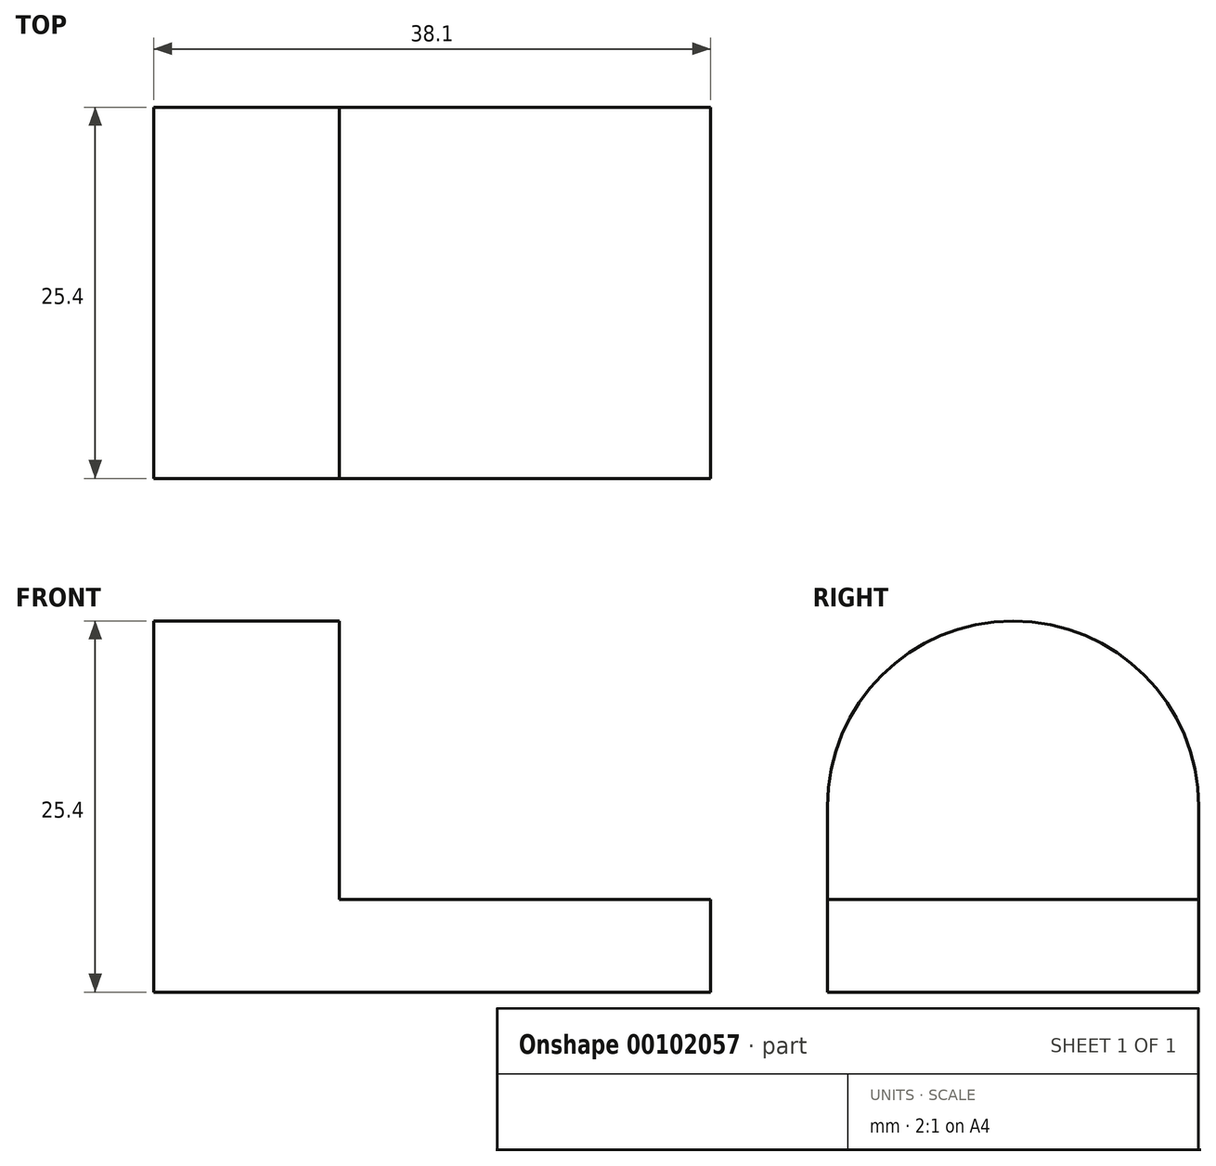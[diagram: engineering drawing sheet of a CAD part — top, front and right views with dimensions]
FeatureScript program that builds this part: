
annotation { "Feature Type Name" : "Feature", "Feature Type Description" : "" }
export const myFeature = defineFeature(function(context is Context, id is Id, definition is map)
    precondition{}
    {
        {
            var Q0;
            Q0=qCreatedBy(makeId("Front.planeOp"),FACE);
            var sketch = newSketch(context, id + "F0", { "sketchPlane" : qUnion([Q0])});
            skLineSegment(sketch, "E0.bottom", {"start": v(0, 0) * mm, "end": v(38.1, 0) * mm});
            skLineSegment(sketch, "E0.top", {"start": v(0, 6.35) * mm, "end": v(38.1, 6.35) * mm});
            skLineSegment(sketch, "E0.left", {"start": v(0, 0) * mm, "end": v(0, 6.35) * mm});
            skLineSegment(sketch, "E0.right", {"start": v(38.1, 0) * mm, "end": v(38.1, 6.35) * mm});
            skSolve(sketch);
        }
        {
            var Q0;
            Q0 = qSketchRegion(id + "F0", true);
            extrude(context, id + "F1", {"entities" : qUnion([Q0]), "depth" : 25.4 * mm});
        }
        {
            var Q0;
            Q0=qCreatedBy(makeId("Right.planeOp"),FACE);
            var sketch = newSketch(context, id + "F2", { "sketchPlane" : qUnion([Q0])});
            skLineSegment(sketch, "E1", {"start": v(-25.4, 6.35) * mm, "end": v(-25.4, 12.7) * mm});
            skLineSegment(sketch, "E2", {"start": v(0, 6.35) * mm, "end": v(0, 12.7) * mm});
            skArc(sketch, "E3", {"start": v(0, 12.7) * mm, "mid": v(-12.7, 25.4) * mm, "end": v(-25.4, 12.7) * mm});
            skLineSegment(sketch, "E4", {"start": v(-25.4, 6.35) * mm, "end": v(0, 6.35) * mm});
            skSolve(sketch);
        }
        {
            var Q0;
            Q0=makeQuery(id+"F2.imprint","IMPRINT",FACE,{"disambiguationData":[TD([[makeQuery(id+"F2.imprint","IMPRINT",EDGE,{"derivedFrom":sQuery(id+"F2.wireOp",EDGE,"E1")}),-1.0]])]});
            extrude(context, id + "F3", {"entities" : qUnion([Q0]), "operationType" : NewBodyOperationType.ADD, "depth" : 12.7 * mm});
        }
    });
